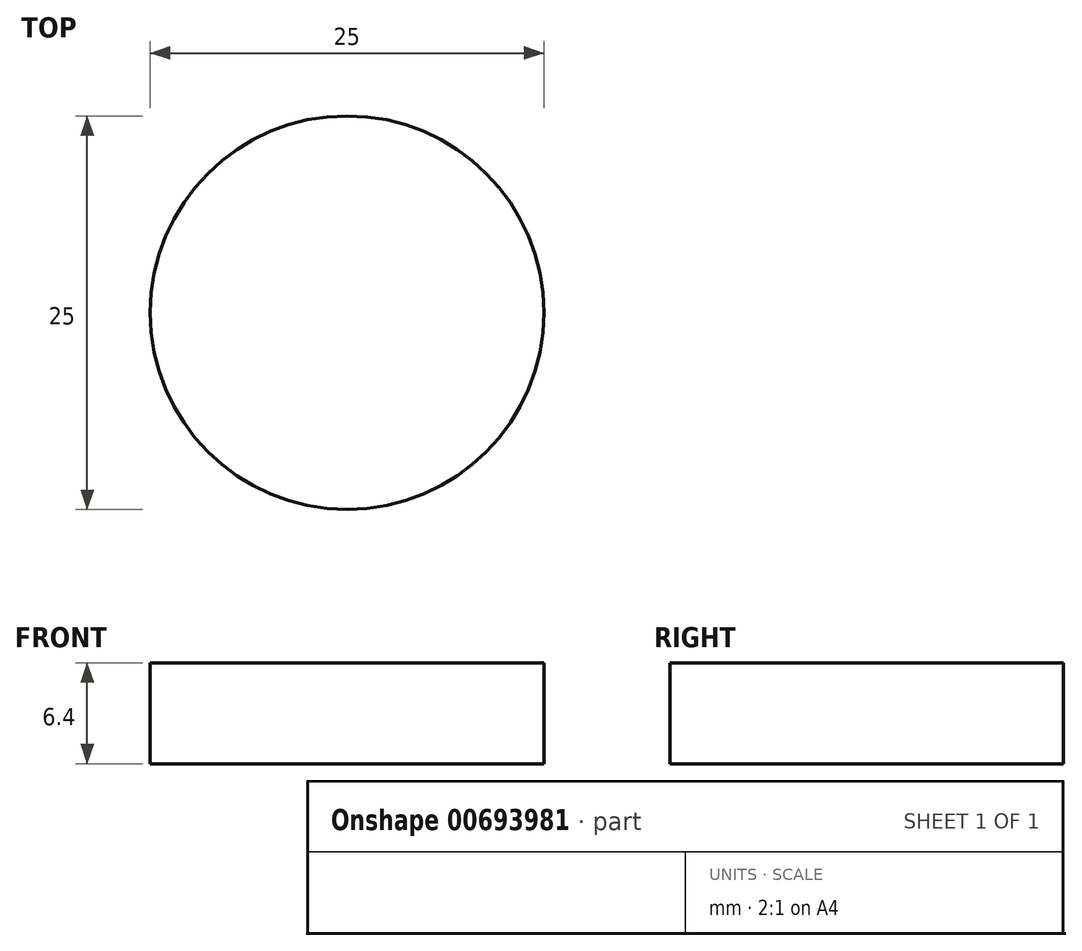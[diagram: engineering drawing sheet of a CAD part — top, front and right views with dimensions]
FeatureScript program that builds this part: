
annotation { "Feature Type Name" : "Feature", "Feature Type Description" : "" }
export const myFeature = defineFeature(function(context is Context, id is Id, definition is map)
    precondition{}
    {
        {
            var Q0;
            Q0=qCreatedBy(makeId("Top.planeOp"),FACE);
            var sketch = newSketch(context, id + "F0", { "sketchPlane" : qUnion([Q0])});
            skCircle(sketch, "E0", {"center": v(0, 0) * mm, "radius": 12.5 * mm});
            skSolve(sketch);
        }
        {
            var Q0;
            Q0 = qSketchRegion(id + "F0", true);
            extrude(context, id + "F1", {"entities" : qUnion([Q0]), "depth" : 6.4 * mm, "offsetDistance" : 25 * mm});
        }
    });
